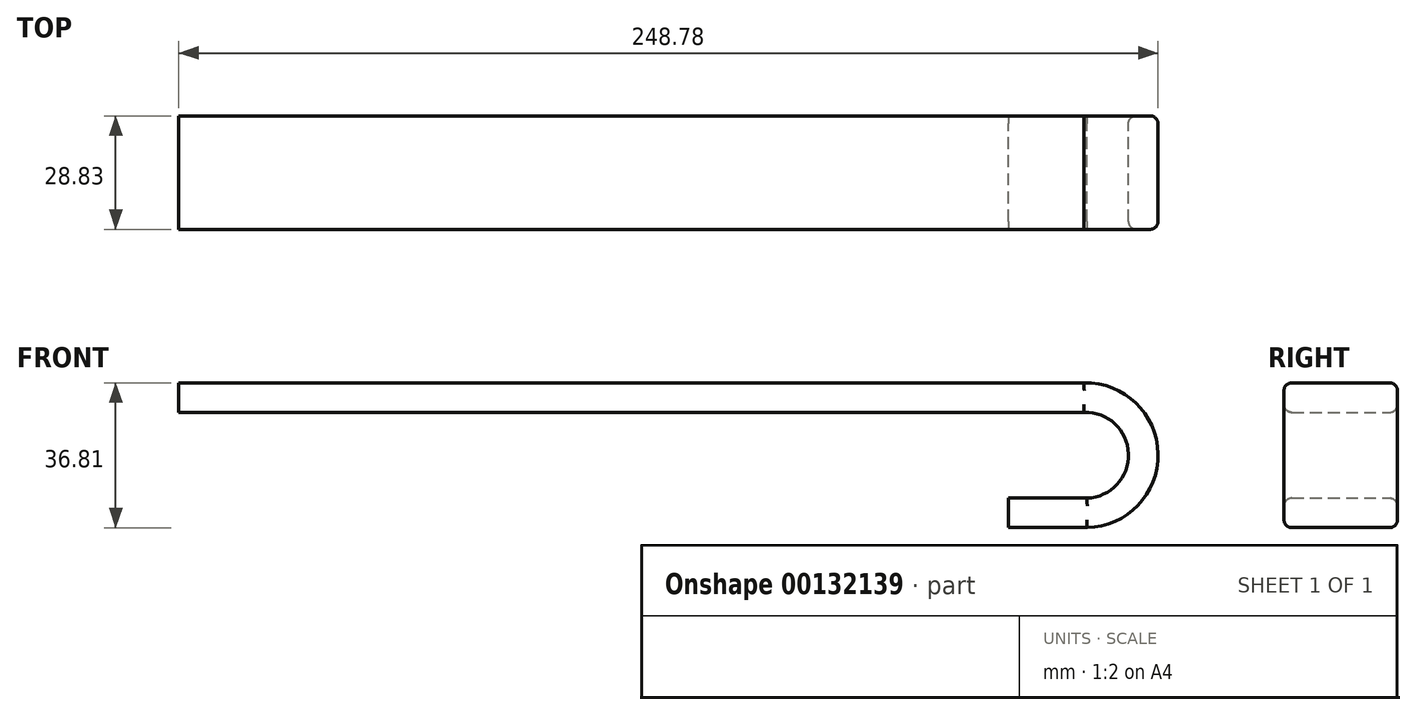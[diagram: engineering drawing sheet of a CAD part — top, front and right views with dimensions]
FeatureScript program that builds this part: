
annotation { "Feature Type Name" : "Feature", "Feature Type Description" : "" }
export const myFeature = defineFeature(function(context is Context, id is Id, definition is map)
    precondition{}
    {
        {
            var Q0;
            Q0=qCreatedBy(makeId("Front.planeOp"),FACE);
            var sketch = newSketch(context, id + "F0", { "sketchPlane" : qUnion([Q0])});
            skLineSegment(sketch, "E0", {"start": v(210.38, -14.05) * mm, "end": v(230.38, -14.05) * mm});
            skArc(sketch, "E1", {"start": v(230.38, -14.05) * mm, "mid": v(245.38, 0.95) * mm, "end": v(230.38, 15.95) * mm});
            skPoint(sketch, "E1.second.point", {"position": v(93.5, 0) * mm});
            skPoint(sketch, "E1.third.point", {"position": v(78.5, 15.16) * mm});
            skLineSegment(sketch, "E2", {"start": v(230.38, 15.95) * mm, "end": v(0.38, 15.95) * mm});
            skSolve(sketch);
        }
        {
            var Q0;
            Q0=qCreatedBy(makeId("Right.planeOp"),FACE);
            var sketch = newSketch(context, id + "F1", { "sketchPlane" : qUnion([Q0])});
            skLineSegment(sketch, "E3.bottom", {"start": v(-14.22, 19.35) * mm, "end": v(14.61, 19.35) * mm});
            skLineSegment(sketch, "E3.top", {"start": v(-14.22, 11.85) * mm, "end": v(14.61, 11.85) * mm});
            skLineSegment(sketch, "E3.left", {"start": v(-14.22, 19.35) * mm, "end": v(-14.22, 11.85) * mm});
            skLineSegment(sketch, "E3.right", {"start": v(14.61, 19.35) * mm, "end": v(14.61, 11.85) * mm});
            skSolve(sketch);
        }
        {
            var Q0;
            Q0=makeQuery(id+"F1.imprint","IMPRINT",FACE,{"disambiguationData":[TD([[makeQuery(id+"F1.imprint","IMPRINT",EDGE,{"derivedFrom":sQuery(id+"F1.wireOp",EDGE,"E3.bottom")}),-1.0]])]});
            var Q1;
            Q1=sQuery(id+"F0.wireOp",EDGE,"E2");
            var Q2;
            Q2=sQuery(id+"F0.wireOp",EDGE,"E1");
            var Q3;
            Q3=sQuery(id+"F0.wireOp",EDGE,"E0");
            sweep(context, id + "F2", {"profiles" : qUnion([Q0]), "path" : qUnion([Q1, Q2, Q3])});
        }
        {
            var Q0;
            Q0=makeQuery(id+"F2.opSweep","SWEPT_EDGE",EDGE,{"disambiguationData":[OSD([sQuery(id+"F0.wireOp",EDGE,"E2"),sQuery(id+"F1.wireOp",EDGE,"E3.top"),sQuery(id+"F1.wireOp",EDGE,"E3.left")])]});
            var Q1;
            Q1=makeQuery(id+"F2.opSweep","SWEPT_EDGE",EDGE,{"disambiguationData":[OSD([sQuery(id+"F0.wireOp",EDGE,"E1"),sQuery(id+"F1.wireOp",EDGE,"E3.top"),sQuery(id+"F1.wireOp",EDGE,"E3.left")])]});
            var Q2;
            Q2=makeQuery(id+"F2.opSweep","SWEPT_EDGE",EDGE,{"disambiguationData":[OSD([sQuery(id+"F0.wireOp",EDGE,"E0"),sQuery(id+"F1.wireOp",EDGE,"E3.top"),sQuery(id+"F1.wireOp",EDGE,"E3.left")])]});
            var Q3;
            Q3=makeQuery(id+"F2.opSweep","SWEPT_EDGE",EDGE,{"disambiguationData":[OSD([sQuery(id+"F0.wireOp",EDGE,"E2"),sQuery(id+"F1.wireOp",EDGE,"E3.bottom"),sQuery(id+"F1.wireOp",EDGE,"E3.left")])]});
            var Q4;
            Q4=makeQuery(id+"F2.opSweep","SWEPT_EDGE",EDGE,{"disambiguationData":[OSD([sQuery(id+"F0.wireOp",EDGE,"E1"),sQuery(id+"F1.wireOp",EDGE,"E3.bottom"),sQuery(id+"F1.wireOp",EDGE,"E3.left")])]});
            var Q5;
            Q5=makeQuery(id+"F2.opSweep","SWEPT_EDGE",EDGE,{"disambiguationData":[OSD([sQuery(id+"F0.wireOp",EDGE,"E0"),sQuery(id+"F1.wireOp",EDGE,"E3.bottom"),sQuery(id+"F1.wireOp",EDGE,"E3.left")])]});
            var Q6;
            Q6=makeQuery(id+"F2.opSweep","SWEPT_EDGE",EDGE,{"disambiguationData":[OSD([sQuery(id+"F0.wireOp",EDGE,"E0"),sQuery(id+"F1.wireOp",EDGE,"E3.top"),sQuery(id+"F1.wireOp",EDGE,"E3.right")])]});
            var Q7;
            Q7=makeQuery(id+"F2.opSweep","SWEPT_EDGE",EDGE,{"disambiguationData":[OSD([sQuery(id+"F0.wireOp",EDGE,"E1"),sQuery(id+"F1.wireOp",EDGE,"E3.top"),sQuery(id+"F1.wireOp",EDGE,"E3.right")])]});
            var Q8;
            Q8=makeQuery(id+"F2.opSweep","SWEPT_EDGE",EDGE,{"disambiguationData":[OSD([sQuery(id+"F0.wireOp",EDGE,"E2"),sQuery(id+"F1.wireOp",EDGE,"E3.top"),sQuery(id+"F1.wireOp",EDGE,"E3.right")])]});
            var Q9;
            Q9=makeQuery(id+"F2.opSweep","SWEPT_EDGE",EDGE,{"disambiguationData":[OSD([sQuery(id+"F0.wireOp",EDGE,"E1"),sQuery(id+"F1.wireOp",EDGE,"E3.bottom"),sQuery(id+"F1.wireOp",EDGE,"E3.right")])]});
            fillet(context, id + "F3", {"entities" : qUnion([Q0, Q1, Q2, Q3, Q4, Q5, Q6, Q7, Q8, Q9]), "radius" : 2 * mm, "tangentPropagation" : true, "allowEdgeOverflow" : false});
        }
    });
